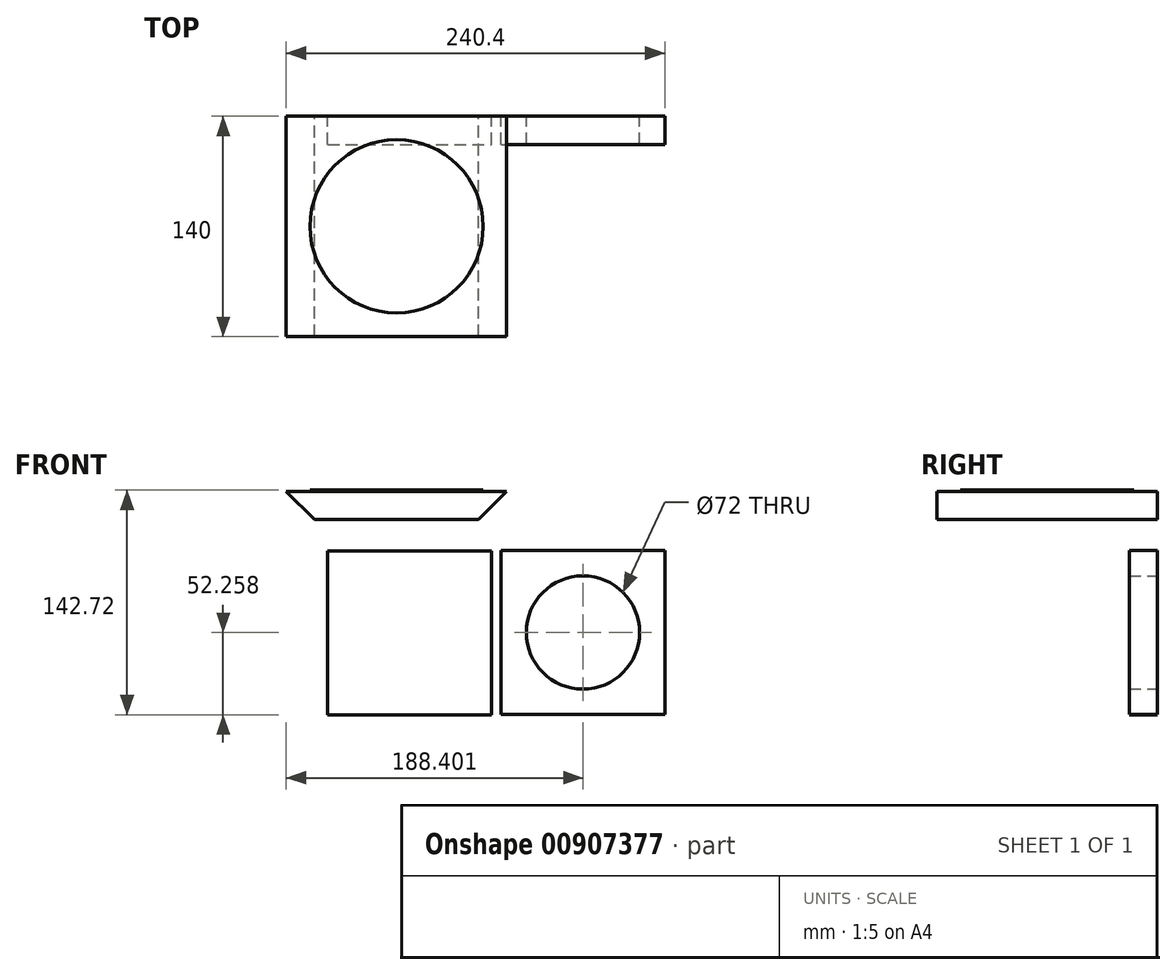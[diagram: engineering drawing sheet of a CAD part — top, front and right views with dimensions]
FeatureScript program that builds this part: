
annotation { "Feature Type Name" : "Feature", "Feature Type Description" : "" }
export const myFeature = defineFeature(function(context is Context, id is Id, definition is map)
    precondition{}
    {
        {
            var Q0;
            Q0=qCreatedBy(makeId("Front.planeOp"),FACE);
            var sketch = newSketch(context, id + "F0", { "sketchPlane" : qUnion([Q0])});
            skLineSegment(sketch, "E0", {"start": v(-52, 0) * mm, "end": v(-70, 18) * mm});
            skLineSegment(sketch, "E1", {"start": v(-70, 18) * mm, "end": v(70, 18) * mm});
            skLineSegment(sketch, "E2", {"start": v(70, 18) * mm, "end": v(52, 0) * mm});
            skLineSegment(sketch, "E3", {"start": v(52, 0) * mm, "end": v(-52, 0) * mm});
            skSolve(sketch);
        }
        {
            var Q0;
            Q0 = qSketchRegion(id + "F0", true);
            extrude(context, id + "F1", {"entities" : qUnion([Q0]), "depth" : 140 * mm, "offsetDistance" : 25 * mm});
        }
        {
            var Q0;
            Q0=qCreatedBy(makeId("Front.planeOp"),FACE);
            var sketch = newSketch(context, id + "F2", { "sketchPlane" : qUnion([Q0])});
            skLineSegment(sketch, "E4.bottom", {"start": v(-43.78, -19.92) * mm, "end": v(60.22, -19.92) * mm});
            skLineSegment(sketch, "E4.top", {"start": v(-43.78, -123.92) * mm, "end": v(60.22, -123.92) * mm});
            skLineSegment(sketch, "E4.left", {"start": v(-43.78, -19.92) * mm, "end": v(-43.78, -123.92) * mm});
            skLineSegment(sketch, "E4.right", {"start": v(60.22, -19.92) * mm, "end": v(60.22, -123.92) * mm});
            skSolve(sketch);
        }
        {
            var Q0;
            Q0 = qSketchRegion(id + "F2", true);
            extrude(context, id + "F3", {"entities" : qUnion([Q0]), "depth" : 18 * mm, "offsetDistance" : 25 * mm});
        }
        {
            var Q0;
            Q0=qCreatedBy(makeId("Front.planeOp"),FACE);
            var sketch = newSketch(context, id + "F4", { "sketchPlane" : qUnion([Q0])});
            skLineSegment(sketch, "E5.bottom", {"start": v(66.4, -19.66) * mm, "end": v(170.4, -19.66) * mm});
            skLineSegment(sketch, "E5.top", {"start": v(66.4, -123.66) * mm, "end": v(170.4, -123.66) * mm});
            skLineSegment(sketch, "E5.left", {"start": v(66.4, -19.66) * mm, "end": v(66.4, -123.66) * mm});
            skLineSegment(sketch, "E5.right", {"start": v(170.4, -19.66) * mm, "end": v(170.4, -123.66) * mm});
            skCircle(sketch, "E6", {"center": v(118.4, -71.66) * mm, "radius": 36 * mm});
            skPoint(sketch, "E6.centerSnap0", {"position": v(118.4, -19.66) * mm});
            skPoint(sketch, "E6.centerSnap1", {"position": v(66.4, -71.66) * mm});
            skSolve(sketch);
        }
        {
            var Q0;
            Q0 = qSketchRegion(id + "F4", true);
            extrude(context, id + "F5", {"entities" : qUnion([Q0]), "depth" : 18 * mm, "offsetDistance" : 25 * mm});
        }
        {
            var Q0;
            Q0=makeQuery(id+"F1.opExtrude","SWEPT_FACE",FACE,{"disambiguationData":[OSD([sQuery(id+"F0.wireOp",EDGE,"E1")])]});
            var sketch = newSketch(context, id + "F6", { "sketchPlane" : qUnion([Q0])});
            skCircle(sketch, "E7", {"center": v(0, -70) * mm, "radius": 55 * mm});
            skPoint(sketch, "E7.centerSnap0", {"position": v(70, -70) * mm});
            skPoint(sketch, "E7.centerSnap1", {"position": v(0, -140) * mm});
            skSolve(sketch);
        }
        {
            var Q0;
            Q0 = qSketchRegion(id + "F6", true);
            extrude(context, id + "F7", {"entities" : qUnion([Q0]), "depth" : 0.8 * mm, "offsetDistance" : 25 * mm});
        }
    });
